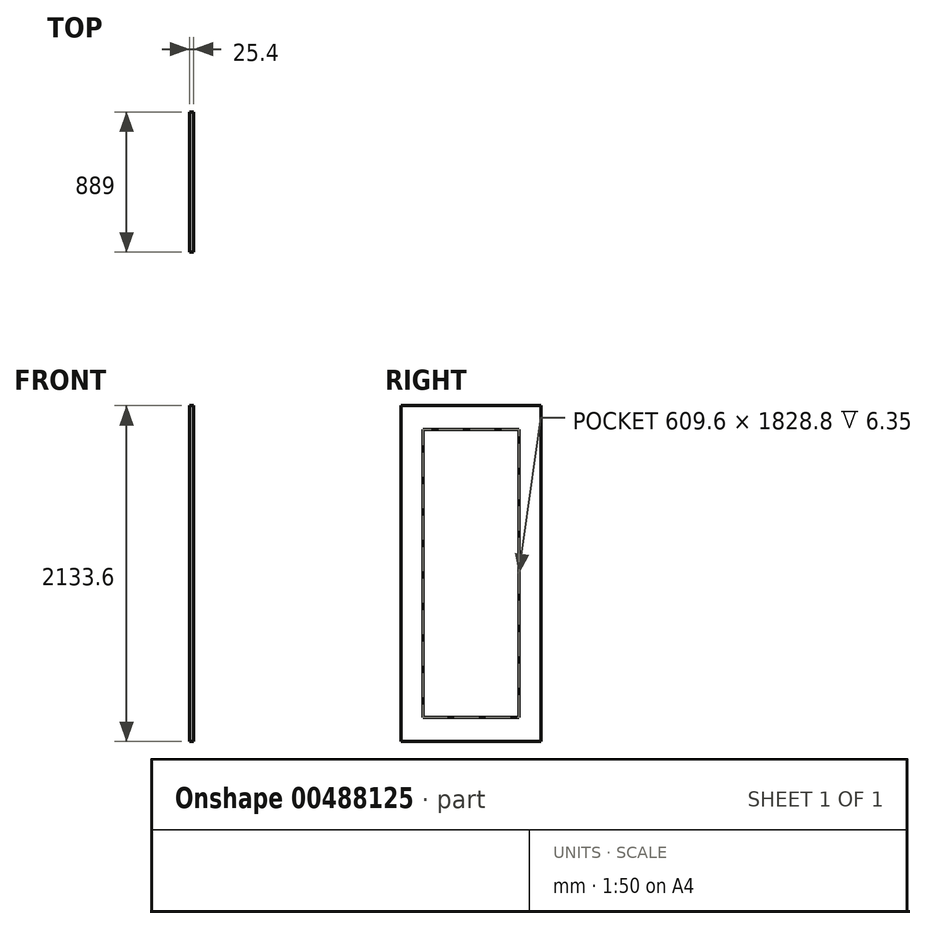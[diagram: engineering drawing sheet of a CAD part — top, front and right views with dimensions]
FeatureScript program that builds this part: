
annotation { "Feature Type Name" : "Feature", "Feature Type Description" : "" }
export const myFeature = defineFeature(function(context is Context, id is Id, definition is map)
    precondition{}
    {
        {
            var Q0;
            Q0=qCreatedBy(makeId("Right.planeOp"),FACE);
            var sketch = newSketch(context, id + "F0", { "sketchPlane" : qUnion([Q0])});
            skLineSegment(sketch, "E0.bottom", {"start": v(444.5, 1066.8) * mm, "end": v(-444.5, 1066.8) * mm});
            skLineSegment(sketch, "E0.top", {"start": v(444.5, -1066.8) * mm, "end": v(-444.5, -1066.8) * mm});
            skLineSegment(sketch, "E0.left", {"start": v(444.5, 1066.8) * mm, "end": v(444.5, -1066.8) * mm});
            skLineSegment(sketch, "E0.right", {"start": v(-444.5, 1066.8) * mm, "end": v(-444.5, -1066.8) * mm});
            skPoint(sketch, "E0.middle", {"position": v(0, 0) * mm});
            skLineSegment(sketch, "E1.bottom", {"start": v(304.8, 914.4) * mm, "end": v(-304.8, 914.4) * mm});
            skLineSegment(sketch, "E1.top", {"start": v(304.8, -914.4) * mm, "end": v(-304.8, -914.4) * mm});
            skLineSegment(sketch, "E1.left", {"start": v(304.8, 914.4) * mm, "end": v(304.8, -914.4) * mm});
            skLineSegment(sketch, "E1.right", {"start": v(-304.8, 914.4) * mm, "end": v(-304.8, -914.4) * mm});
            skSolve(sketch);
        }
        {
            var Q0;
            Q0=makeQuery(id+"F0.imprint","IMPRINT",FACE,{"disambiguationData":[TD([[makeQuery(id+"F0.imprint","IMPRINT",EDGE,{"derivedFrom":sQuery(id+"F0.wireOp",EDGE,"E1.bottom")}),1.0]])]});
            extrude(context, id + "F1", {"entities" : qUnion([Q0]), "depth" : 19.05 * mm, "offsetDistance" : 25.4 * mm});
        }
        {
            var Q0;
            Q0=makeQuery(id+"F0.imprint","IMPRINT",FACE,{"disambiguationData":[TD([[makeQuery(id+"F0.imprint","IMPRINT",EDGE,{"derivedFrom":sQuery(id+"F0.wireOp",EDGE,"E0.bottom")}),1.0]])]});
            extrude(context, id + "F2", {"entities" : qUnion([Q0]), "operationType" : NewBodyOperationType.ADD, "depth" : 25.4 * mm, "offsetDistance" : 25.4 * mm});
        }
    });
